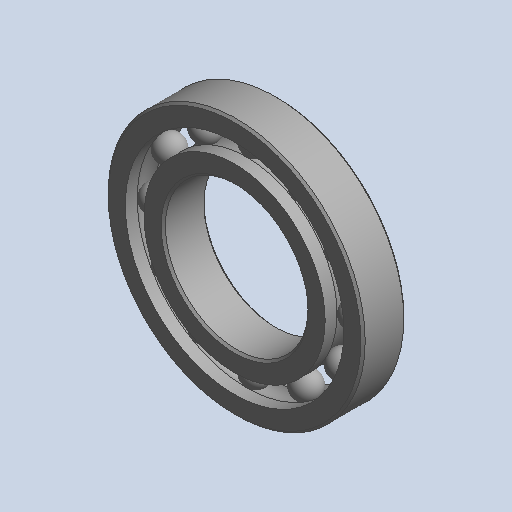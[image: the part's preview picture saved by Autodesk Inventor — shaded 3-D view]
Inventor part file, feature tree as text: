
AUTODESK INVENTOR PART (.ipt)
format: ipt  version: 2022.3 (Build 263350000, 350)  size: 538,624 bytes
history: native  units: mm (DEFAULTED — no unit token found)
features: other x11, revolve x3
ambient origin geometry x8: Origin, YZ Plane, XZ Plane, XY Plane, X Axis, Y Axis, Z Axis, Center Point
bodies: Solid1 (feature_tree), Solid2 (feature_tree), Solid3 (feature_tree), Solid4 (feature_tree), Solid5 (feature_tree), Solid6 (feature_tree), Solid7 (feature_tree), Solid8 (feature_tree), Solid9 (feature_tree), Solid10 (feature_tree), Solid11 (feature_tree), Solid12 (feature_tree), Solid13 (feature_tree), Solid14 (feature_tree)
feature tree (14):
  revolve  "Revolve1"  [1 undecoded]
  revolve  "Revolve3"  [1 undecoded]
  revolve  "Revolve4"  [1 undecoded]
  other  "CirPattern1[1]"
  other  "CirPattern1[2]"
  other  "CirPattern1[3]"
  other  "CirPattern1[4]"
  other  "CirPattern1[5]"
  other  "CirPattern1[6]"
  other  "CirPattern1[7]"
  other  "CirPattern1[8]"
  other  "CirPattern1[9]"
  other  "CirPattern1[10]"
  other  "CirPattern1[11]"
note: 3 required parameter values undecoded (feature->parameter linkage not recoverable at this tier; creation-order binding heuristic only, values carry confidence <= 0.55)
